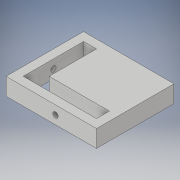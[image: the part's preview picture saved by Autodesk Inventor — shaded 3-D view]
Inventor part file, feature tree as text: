
AUTODESK INVENTOR PART (.ipt)
format: ipt  version: 2019 (Build 230136000, 136)  size: 125,440 bytes
history: native  units: in
note: dims shown in document units (in); Inventor stores cm internally (conversion verified against a paired STEP export)
features: sketch x3, hole x2, extrude x1
ambient origin geometry x8: Origin, YZ Plane, XZ Plane, XY Plane, X Axis, Y Axis, Z Axis, Center Point
bodies: Solid1 (feature_tree)
feature tree (6):
  extrude  "Extrusion1"  Depth=5.25in
  hole  "Hole1"  [1 undecoded]
  hole  "Hole2"  [1 undecoded]
  sketch  "Sketch1"  dims[d0=4.5in d1=5.25in]
  sketch  "Sketch3"  dims[d2=0.5in d3=0.5in]
  sketch  "Sketch4"  dims[d4=0.5in d5=0.5in d6=0.75in d7=0.75in d8=1.0in d9=0.0in d10=4.75in d11=1.0in d12=2.375in d13=0.5in d14=0.3091in d15=0.276in d16=0.375in d17=0.25in d18=0.5635in d19=1.0in d20=0.8108in d21=1.0in d22=4.5in d23=0.5in d24=2.25in d25=0.3091in d26=0.276in d27=0.375in d28=0.25in d29=0.5635in d30=1.0in d31=0.0in]
note: 2 required parameter values undecoded (feature->parameter linkage not recoverable at this tier; creation-order binding heuristic only, values carry confidence <= 0.55)
